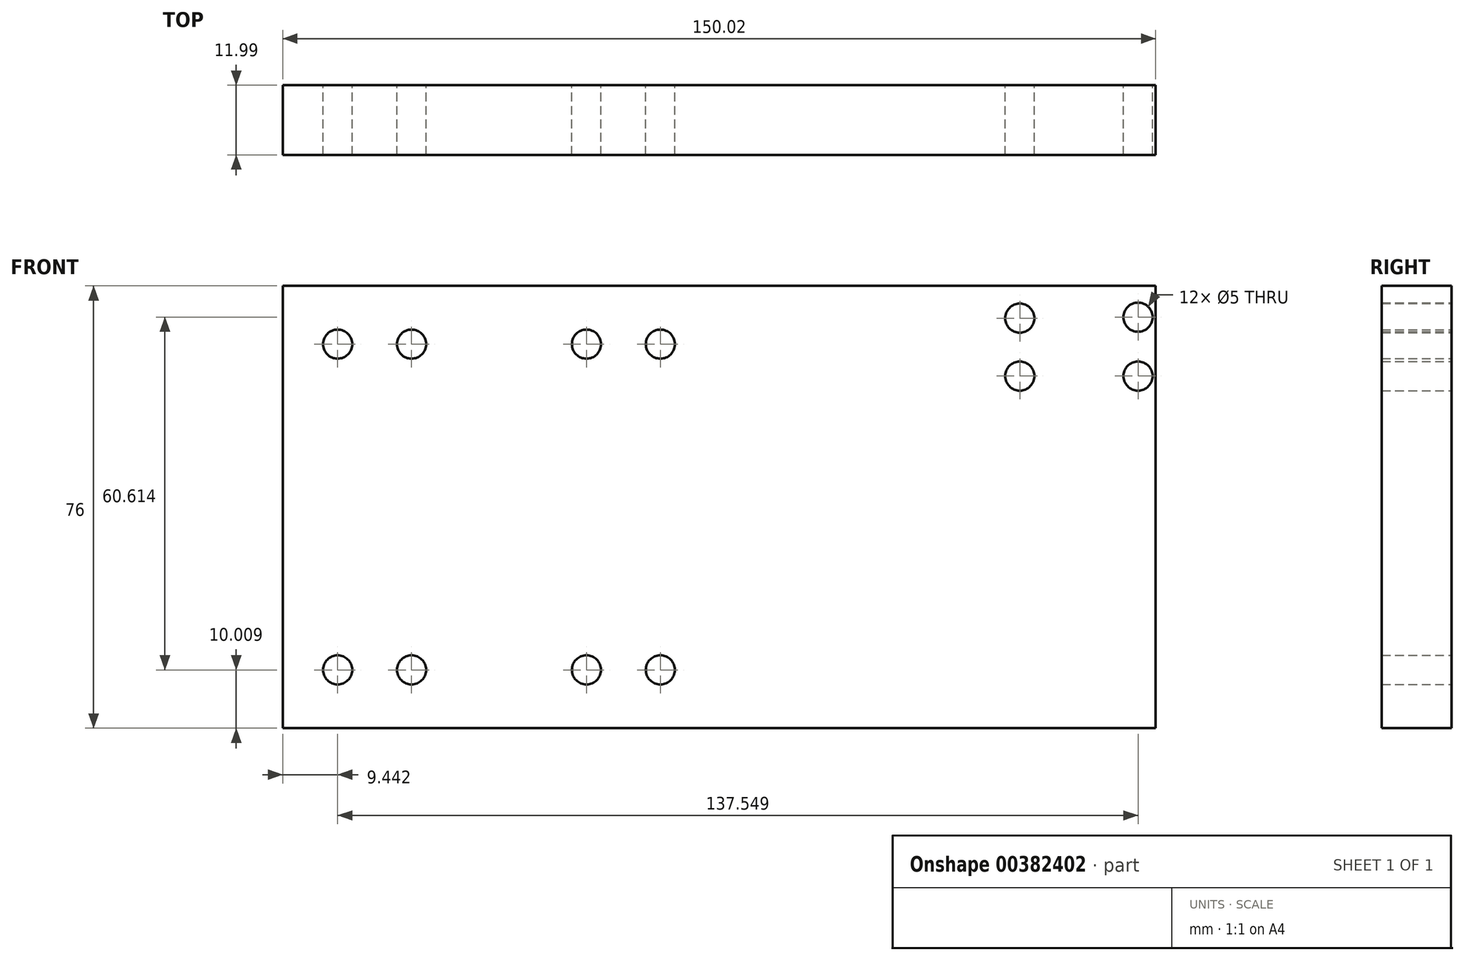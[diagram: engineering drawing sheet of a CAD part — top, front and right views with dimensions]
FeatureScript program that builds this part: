
annotation { "Feature Type Name" : "Feature", "Feature Type Description" : "" }
export const myFeature = defineFeature(function(context is Context, id is Id, definition is map)
    precondition{}
    {
        {
            var Q0;
            Q0=qCreatedBy(makeId("Front.planeOp"),FACE);
            var sketch = newSketch(context, id + "F0", { "sketchPlane" : qUnion([Q0])});
            skLineSegment(sketch, "E0.bottom", {"start": v(75, -38) * mm, "end": v(-75, -38) * mm});
            skLineSegment(sketch, "E0.top", {"start": v(75, 38) * mm, "end": v(-75, 38) * mm});
            skLineSegment(sketch, "E0.left", {"start": v(75, -38) * mm, "end": v(75, 38) * mm});
            skLineSegment(sketch, "E0.right", {"start": v(-75, -38) * mm, "end": v(-75, 38) * mm});
            skPoint(sketch, "E0.middle", {"position": v(0, 0) * mm});
            skCircle(sketch, "E1", {"center": v(-65.57, 28) * mm, "radius": 2.5 * mm});
            skCircle(sketch, "E2", {"center": v(-52.87, 28) * mm, "radius": 2.5 * mm});
            skCircle(sketch, "E3", {"center": v(-22.8, 28) * mm, "radius": 2.5 * mm});
            skCircle(sketch, "E4", {"center": v(-10.1, 28) * mm, "radius": 2.5 * mm});
            skCircle(sketch, "E5", {"center": v(-65.57, -28) * mm, "radius": 2.5 * mm});
            skCircle(sketch, "E6", {"center": v(-52.87, -28) * mm, "radius": 2.5 * mm});
            skCircle(sketch, "E7", {"center": v(-22.8, -28) * mm, "radius": 2.5 * mm});
            skCircle(sketch, "E8", {"center": v(-10.1, -28) * mm, "radius": 2.5 * mm});
            skCircle(sketch, "E9", {"center": v(71.98, 22.5) * mm, "radius": 2.5 * mm});
            skCircle(sketch, "E10", {"center": v(51.66, 22.5) * mm, "radius": 2.5 * mm});
            skCircle(sketch, "E11", {"center": v(51.66, 32.45) * mm, "radius": 2.5 * mm});
            skCircle(sketch, "E12", {"center": v(71.98, 32.62) * mm, "radius": 2.5 * mm});
            skSolve(sketch);
        }
        {
            var Q0;
            Q0=makeQuery(id+"F0.imprint","IMPRINT",FACE,{"disambiguationData":[TD([[makeQuery(id+"F0.imprint","IMPRINT",EDGE,{"derivedFrom":sQuery(id+"F0.wireOp",EDGE,"E0.bottom")}),-1.0]])]});
            extrude(context, id + "F1", {"entities" : qUnion([Q0]), "depth" : 12 * mm});
        }
    });
